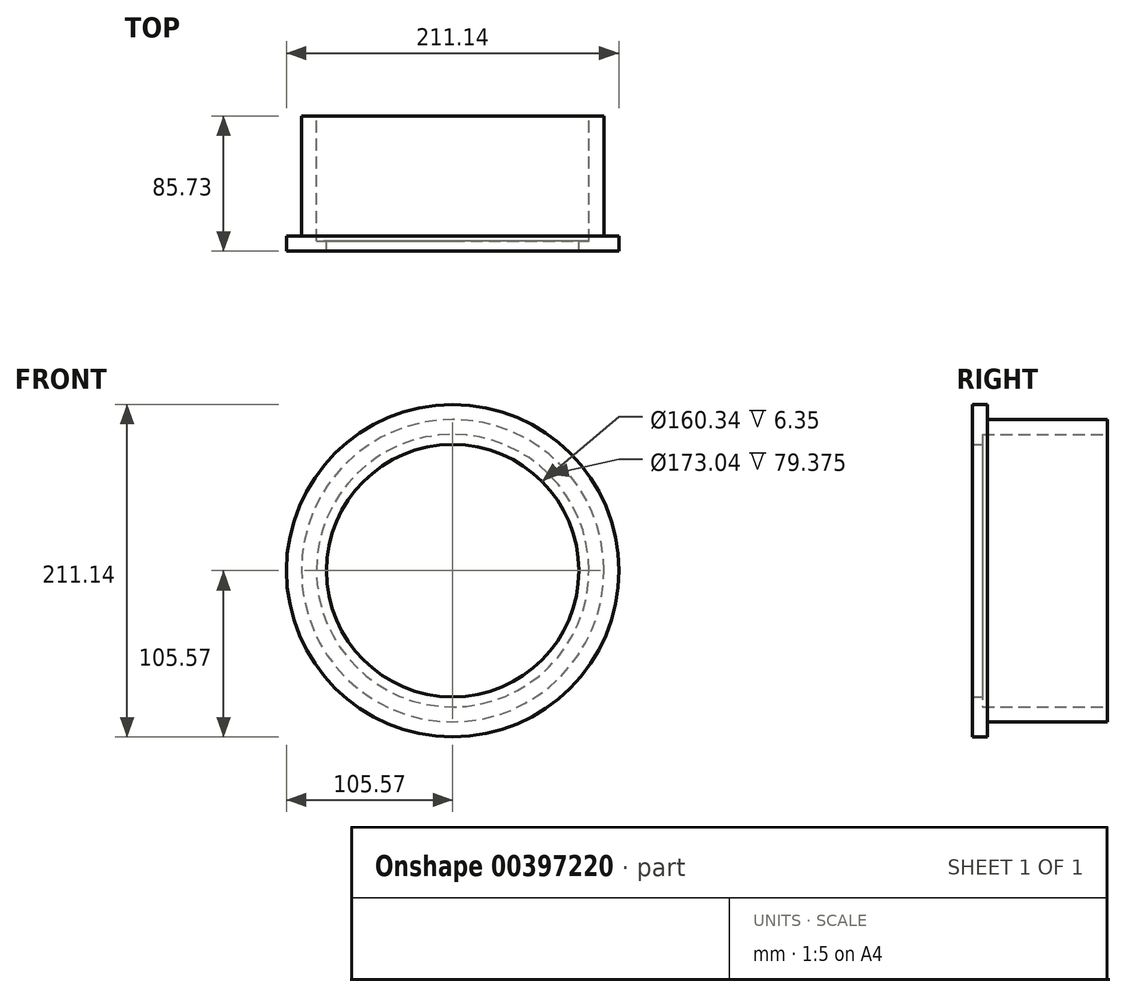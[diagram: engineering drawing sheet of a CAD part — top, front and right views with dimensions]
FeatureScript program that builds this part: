
annotation { "Feature Type Name" : "Feature", "Feature Type Description" : "" }
export const myFeature = defineFeature(function(context is Context, id is Id, definition is map)
    precondition{}
    {
        {
            var Q0;
            Q0=qCreatedBy(makeId("Right.planeOp"),FACE);
            var sketch = newSketch(context, id + "F0", { "sketchPlane" : qUnion([Q0])});
            skLineSegment(sketch, "E0", {"start": v(52.3, 0) * mm, "end": v(-59.41, 0) * mm, "construction": true});
            skLineSegment(sketch, "E1", {"start": v(0, 63.56) * mm, "end": v(0, -63.72) * mm, "construction": true});
            skLineSegment(sketch, "E2", {"start": v(0, 80.17) * mm, "end": v(6.35, 80.17) * mm});
            skLineSegment(sketch, "E3", {"start": v(6.35, 80.17) * mm, "end": v(6.35, 86.52) * mm});
            skLineSegment(sketch, "E4", {"start": v(6.35, 86.52) * mm, "end": v(85.73, 86.52) * mm});
            skLineSegment(sketch, "E5", {"start": v(85.73, 86.52) * mm, "end": v(85.73, 96.04) * mm});
            skLineSegment(sketch, "E6", {"start": v(85.73, 96.04) * mm, "end": v(9.52, 96.04) * mm});
            skLineSegment(sketch, "E7", {"start": v(9.52, 96.04) * mm, "end": v(9.52, 105.57) * mm});
            skLineSegment(sketch, "E8", {"start": v(9.53, 105.57) * mm, "end": v(0, 105.57) * mm});
            skLineSegment(sketch, "E9", {"start": v(0, 105.57) * mm, "end": v(0, 80.17) * mm});
            skSolve(sketch);
        }
        {
            var Q0;
            Q0=qSketchRegion(id+"F0",true);
            var Q1;
            Q1=sQuery(id+"F0.wireOp",EDGE,"E0");
            revolve(context, id + "F1", {"entities" : qUnion([Q0]), "axis" : qUnion([Q1]), "revolveType" : RevolveType.FULL});
        }
    });
